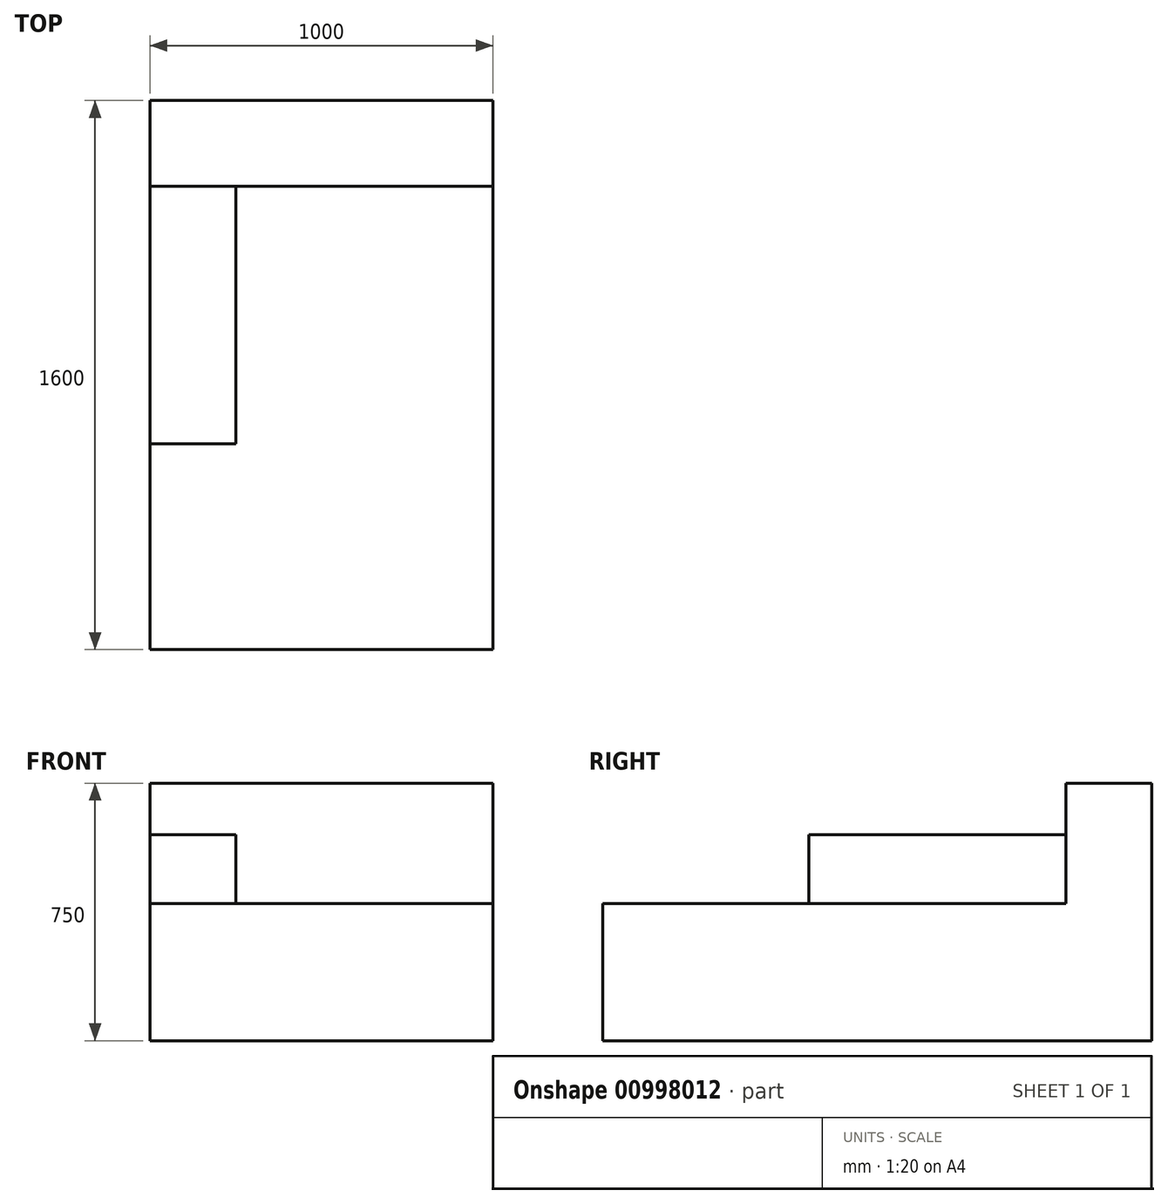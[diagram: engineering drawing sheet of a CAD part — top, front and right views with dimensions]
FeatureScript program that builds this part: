
annotation { "Feature Type Name" : "Feature", "Feature Type Description" : "" }
export const myFeature = defineFeature(function(context is Context, id is Id, definition is map)
    precondition{}
    {
        {
            var Q0;
            Q0=qCreatedBy(makeId("Top.planeOp"),FACE);
            var sketch = newSketch(context, id + "F0", { "sketchPlane" : qUnion([Q0])});
            skLineSegment(sketch, "E0.bottom", {"start": v(-500, 800) * mm, "end": v(500, 800) * mm});
            skLineSegment(sketch, "E0.top", {"start": v(-500, -800) * mm, "end": v(500, -800) * mm});
            skLineSegment(sketch, "E0.left", {"start": v(-500, 800) * mm, "end": v(-500, -800) * mm});
            skLineSegment(sketch, "E0.right", {"start": v(500, 800) * mm, "end": v(500, -800) * mm});
            skLineSegment(sketch, "E1", {"start": v(0, 0) * mm, "end": v(0, 739.26) * mm, "construction": true});
            skLineSegment(sketch, "E2", {"start": v(0, 0) * mm, "end": v(-673.82, 0) * mm, "construction": true});
            skSolve(sketch);
        }
        {
            var Q0;
            Q0 = qSketchRegion(id + "F0", true);
            extrude(context, id + "F1", {"entities" : qUnion([Q0]), "depth" : 750 * mm, "offsetDistance" : 25 * mm});
        }
        {
            var Q0;
            Q0=makeQuery(id+"F1.opExtrude","CAP_FACE",FACE,{"disambiguationData":[OSD([sQuery(id+"F0.wireOp",EDGE,"E0.bottom"),sQuery(id+"F0.wireOp",EDGE,"E0.top"),sQuery(id+"F0.wireOp",EDGE,"E0.left"),sQuery(id+"F0.wireOp",EDGE,"E0.right")])],"isStart":false});
            var sketch = newSketch(context, id + "F2", { "sketchPlane" : qUnion([Q0])});
            skLineSegment(sketch, "E3", {"start": v(-500, -200) * mm, "end": v(-250, -200) * mm});
            skLineSegment(sketch, "E4", {"start": v(-250, -200) * mm, "end": v(-250, 550) * mm});
            skLineSegment(sketch, "E5", {"start": v(-250, 550) * mm, "end": v(500, 550) * mm});
            skLineSegment(sketch, "E6", {"start": v(500, 550) * mm, "end": v(500, -800) * mm});
            skLineSegment(sketch, "E7", {"start": v(500, -800) * mm, "end": v(-500, -800) * mm});
            skLineSegment(sketch, "E8", {"start": v(-500, -800) * mm, "end": v(-500, -200) * mm});
            skSolve(sketch);
        }
        {
            var Q0;
            Q0=makeQuery(id+"F2.imprint","IMPRINT",FACE,{"disambiguationData":[TD([[makeQuery(id+"F2.imprint","IMPRINT",EDGE,{"derivedFrom":sQuery(id+"F2.wireOp",EDGE,"E3")}),-1.0]])]});
            extrude(context, id + "F3", {"entities" : qUnion([Q0]), "operationType" : NewBodyOperationType.REMOVE, "oppositeDirection" : true, "depth" : 350 * mm, "offsetDistance" : 25 * mm});
        }
        {
            var Q0;
            Q0=makeQuery(id+"F1.opExtrude","CAP_FACE",FACE,{"disambiguationData":[OSD([sQuery(id+"F0.wireOp",EDGE,"E0.bottom"),sQuery(id+"F0.wireOp",EDGE,"E0.top"),sQuery(id+"F0.wireOp",EDGE,"E0.left"),sQuery(id+"F0.wireOp",EDGE,"E0.right")])],"isStart":false});
            var sketch = newSketch(context, id + "F4", { "sketchPlane" : qUnion([Q0])});
            skLineSegment(sketch, "E9", {"start": v(-250, 550) * mm, "end": v(-500, 550) * mm});
            skSolve(sketch);
        }
        {
            var Q0;
            Q0 = qSketchRegion(id + "F4", true);
            var Q1;
            {var subQ0=sQuery(id+"F4.wireOp",EDGE,"E9");Q1=makeQuery(id+"F4.imprint","IMPRINT",FACE,{"disambiguationData":[TD([[makeQuery(id+"F4.imprint","IMPRINT",EDGE,{"derivedFrom":subQ0}),1.0]])]});}
            extrude(context, id + "F5", {"entities" : qUnion([Q0, Q1]), "operationType" : NewBodyOperationType.REMOVE, "oppositeDirection" : true, "depth" : 150 * mm, "offsetDistance" : 25 * mm});
        }
    });
